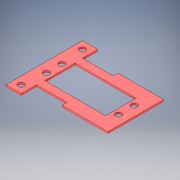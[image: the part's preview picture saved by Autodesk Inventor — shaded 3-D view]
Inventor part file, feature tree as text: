
AUTODESK INVENTOR PART (.ipt)
format: ipt  version: 2019 (Build 230136000, 136)  size: 161,792 bytes
history: native  units: mm
features: other x1, extrude x1, sketch x1
ambient origin geometry x8: Origin, YZ Plane, XZ Plane, XY Plane, X Axis, Y Axis, Z Axis, Center Point
bodies: Body1 (feature_tree)
feature tree (3):
  other  "Sólido1"
  extrude  "Extrusión1"  Depth=1.0mm
  sketch  "Boceto1"  dims[d0=10.0mm d1=9.91mm d2=19.82mm d3=9.66mm d4=39.88mm d5=4.0mm d6=4.0mm d7=4.0mm d8=5.085mm d9=10.17mm d10=13.47mm d11=13.47mm d12=4.0mm d13=33.79mm d14=33.79mm d15=5.085mm d16=10.17mm d25=15.0mm d26=30.0mm d27=60.0mm d28=40.0mm d29=10.0mm d30=10.0mm d31=10.0mm d32=4.0mm d33=4.0mm d34=5.0mm d35=5.0mm d36=5.0mm d37=5.0mm d38=3.18mm d39=30.0mm d40=1.0mm d41=0.0mm]
